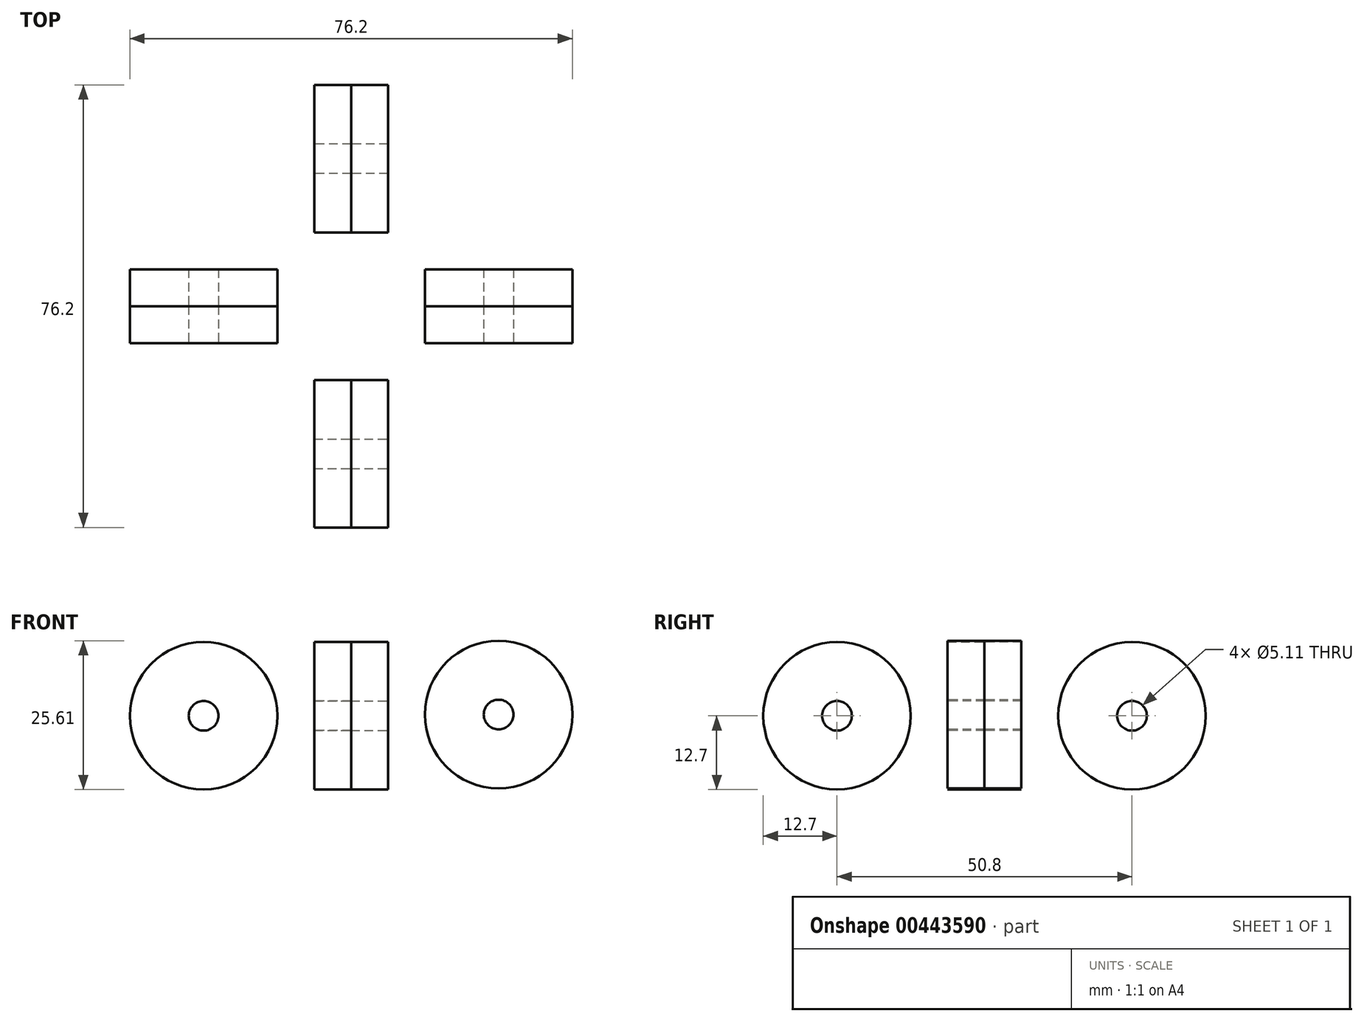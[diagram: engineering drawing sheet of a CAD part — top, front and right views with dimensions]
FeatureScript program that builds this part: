
annotation { "Feature Type Name" : "Feature", "Feature Type Description" : "" }
export const myFeature = defineFeature(function(context is Context, id is Id, definition is map)
    precondition{}
    {
        {
            var Q0;
            Q0=qCreatedBy(makeId("Front.planeOp"),FACE);
            var sketch = newSketch(context, id + "F0", { "sketchPlane" : qUnion([Q0])});
            skCircle(sketch, "E0", {"center": v(25.4, 0.21) * mm, "radius": 12.7 * mm});
            skCircle(sketch, "E1", {"center": v(-25.4, 0) * mm, "radius": 12.7 * mm});
            skSolve(sketch);
        }
        {
            var Q0;
            Q0 = qSketchRegion(id + "F0", true);
            extrude(context, id + "F1", {"entities" : qUnion([Q0]), "depth" : 6.35 * mm});
        }
        {
            var Q0;
            Q0=makeQuery(id+"F1.opExtrude","CAP_FACE",FACE,{"disambiguationData":[OSD([sQuery(id+"F0.wireOp",EDGE,"E1")])],"isStart":true});
            var Q1;
            Q1=makeQuery(id+"F1.opExtrude","CAP_FACE",FACE,{"disambiguationData":[OSD([sQuery(id+"F0.wireOp",EDGE,"E0")])],"isStart":true});
            extrude(context, id + "F2", {"entities" : qUnion([Q0, Q1]), "depth" : 6.35 * mm});
        }
        {
            var Q0;
            Q0=makeQuery(id+"F1.opExtrude","CAP_FACE",FACE,{"disambiguationData":[OSD([sQuery(id+"F0.wireOp",EDGE,"E1")])],"isStart":false});
            var sketch = newSketch(context, id + "F3", { "sketchPlane" : qUnion([Q0])});
            skCircle(sketch, "E2", {"center": v(-25.4, 0) * mm, "radius": 2.55 * mm});
            skSolve(sketch);
        }
        {
            var Q0;
            Q0 = qSketchRegion(id + "F3", true);
            extrude(context, id + "F4", {"entities" : qUnion([Q0]), "operationType" : NewBodyOperationType.REMOVE, "oppositeDirection" : true, "depth" : 50.8 * mm});
        }
        {
            var Q0;
            Q0=makeQuery(id+"F2.opExtrude","CAP_FACE",FACE,{"disambiguationData":[OSD([sQuery(id+"F0.wireOp",EDGE,"E1")])],"isStart":false});
            var sketch = newSketch(context, id + "F5", { "sketchPlane" : qUnion([Q0])});
            skCircle(sketch, "E3", {"center": v(25.4, 0) * mm, "radius": 2.55 * mm});
            skSolve(sketch);
        }
        {
            var Q0;
            Q0 = qSketchRegion(id + "F5", true);
            extrude(context, id + "F6", {"entities" : qUnion([Q0]), "operationType" : NewBodyOperationType.REMOVE, "oppositeDirection" : true, "depth" : 25.4 * mm});
        }
        {
            var Q0;
            Q0=makeQuery(id+"F1.opExtrude","CAP_FACE",FACE,{"disambiguationData":[OSD([sQuery(id+"F0.wireOp",EDGE,"E0")])],"isStart":false});
            var sketch = newSketch(context, id + "F7", { "sketchPlane" : qUnion([Q0])});
            skCircle(sketch, "E4", {"center": v(25.4, 0.21) * mm, "radius": 2.55 * mm});
            skSolve(sketch);
        }
        {
            var Q0;
            Q0 = qSketchRegion(id + "F7", true);
            extrude(context, id + "F8", {"entities" : qUnion([Q0]), "operationType" : NewBodyOperationType.REMOVE, "oppositeDirection" : true, "depth" : 25.4 * mm});
        }
        {
            var Q0;
            Q0=makeQuery(id+"F2.opExtrude","CAP_FACE",FACE,{"disambiguationData":[OSD([sQuery(id+"F0.wireOp",EDGE,"E0")])],"isStart":false});
            var sketch = newSketch(context, id + "F9", { "sketchPlane" : qUnion([Q0])});
            skCircle(sketch, "E5", {"center": v(-25.4, 0.21) * mm, "radius": 2.55 * mm});
            skSolve(sketch);
        }
        {
            var Q0;
            Q0 = qSketchRegion(id + "F9", true);
            extrude(context, id + "F10", {"entities" : qUnion([Q0]), "operationType" : NewBodyOperationType.REMOVE, "oppositeDirection" : true, "depth" : 25.4 * mm});
        }
        {
            var Q0;
            Q0=qCreatedBy(makeId("Right.planeOp"),FACE);
            var sketch = newSketch(context, id + "F11", { "sketchPlane" : qUnion([Q0])});
            skCircle(sketch, "E6", {"center": v(-25.4, 0) * mm, "radius": 12.7 * mm});
            skCircle(sketch, "E7", {"center": v(25.4, 0) * mm, "radius": 12.7 * mm});
            skSolve(sketch);
        }
        {
            var Q0;
            Q0 = qSketchRegion(id + "F11", true);
            extrude(context, id + "F12", {"entities" : qUnion([Q0]), "depth" : 6.35 * mm});
        }
        {
            var Q0;
            Q0=makeQuery(id+"F12.opExtrude","CAP_FACE",FACE,{"disambiguationData":[OSD([sQuery(id+"F11.wireOp",EDGE,"E7")])],"isStart":true});
            var Q1;
            Q1=makeQuery(id+"F12.opExtrude","CAP_FACE",FACE,{"disambiguationData":[OSD([sQuery(id+"F11.wireOp",EDGE,"E6")])],"isStart":true});
            extrude(context, id + "F13", {"entities" : qUnion([Q0, Q1]), "depth" : 6.35 * mm});
        }
        {
            var Q0;
            Q0=makeQuery(id+"F13.opExtrude","CAP_FACE",FACE,{"disambiguationData":[OSD([sQuery(id+"F11.wireOp",EDGE,"E7")])],"isStart":false});
            var sketch = newSketch(context, id + "F14", { "sketchPlane" : qUnion([Q0])});
            skCircle(sketch, "E8", {"center": v(-25.4, 0) * mm, "radius": 2.55 * mm});
            skSolve(sketch);
        }
        {
            var Q0;
            Q0 = qSketchRegion(id + "F14", true);
            extrude(context, id + "F15", {"entities" : qUnion([Q0]), "operationType" : NewBodyOperationType.REMOVE, "oppositeDirection" : true, "depth" : 25.4 * mm});
        }
        {
            var Q0;
            Q0=makeQuery(id+"F12.opExtrude","CAP_FACE",FACE,{"disambiguationData":[OSD([sQuery(id+"F11.wireOp",EDGE,"E7")])],"isStart":false});
            var sketch = newSketch(context, id + "F16", { "sketchPlane" : qUnion([Q0])});
            skCircle(sketch, "E9", {"center": v(25.4, 0) * mm, "radius": 2.55 * mm});
            skSolve(sketch);
        }
        {
            var Q0;
            Q0 = qSketchRegion(id + "F16", true);
            extrude(context, id + "F17", {"entities" : qUnion([Q0]), "operationType" : NewBodyOperationType.REMOVE, "oppositeDirection" : true, "depth" : 25.4 * mm});
        }
        {
            var Q0;
            Q0=makeQuery(id+"F12.opExtrude","CAP_FACE",FACE,{"disambiguationData":[OSD([sQuery(id+"F11.wireOp",EDGE,"E6")])],"isStart":false});
            var sketch = newSketch(context, id + "F18", { "sketchPlane" : qUnion([Q0])});
            skCircle(sketch, "E10", {"center": v(-25.4, 0) * mm, "radius": 2.55 * mm});
            skSolve(sketch);
        }
        {
            var Q0;
            Q0 = qSketchRegion(id + "F18", true);
            extrude(context, id + "F19", {"entities" : qUnion([Q0]), "operationType" : NewBodyOperationType.REMOVE, "oppositeDirection" : true, "depth" : 25.4 * mm});
        }
        {
            var Q0;
            Q0=makeQuery(id+"F13.opExtrude","CAP_FACE",FACE,{"disambiguationData":[OSD([sQuery(id+"F11.wireOp",EDGE,"E6")])],"isStart":false});
            var sketch = newSketch(context, id + "F20", { "sketchPlane" : qUnion([Q0])});
            skCircle(sketch, "E11", {"center": v(25.4, 0) * mm, "radius": 2.55 * mm});
            skSolve(sketch);
        }
        {
            var Q0;
            Q0 = qSketchRegion(id + "F20", true);
            extrude(context, id + "F21", {"entities" : qUnion([Q0]), "operationType" : NewBodyOperationType.REMOVE, "oppositeDirection" : true, "depth" : 25.4 * mm});
        }
    });
